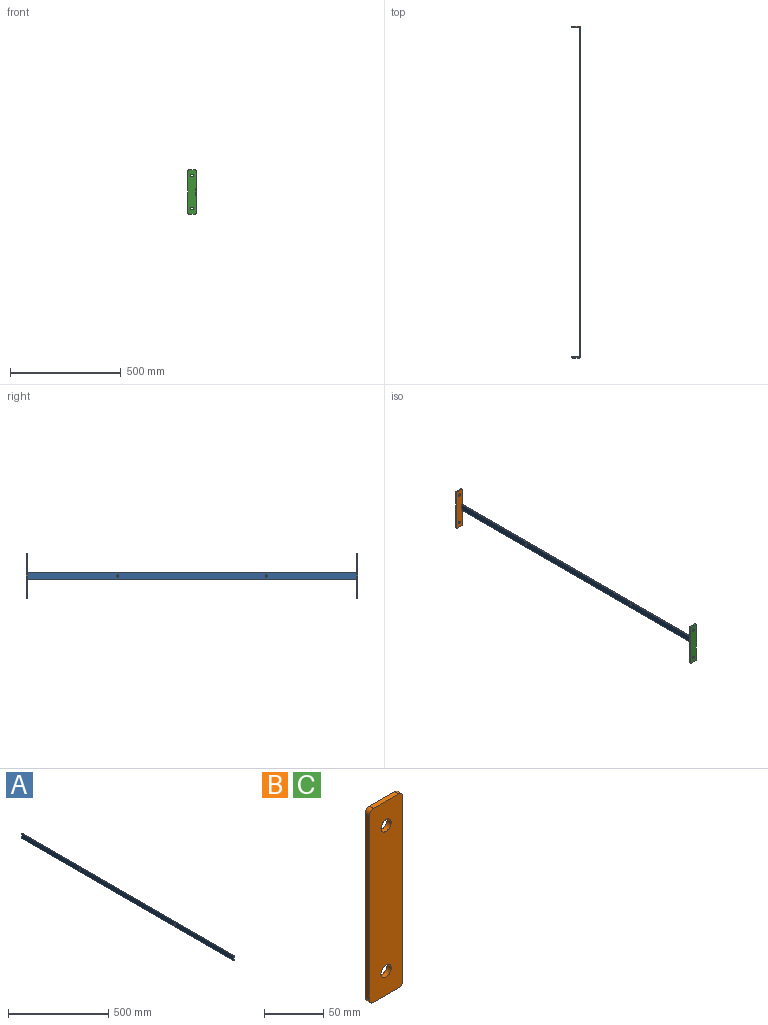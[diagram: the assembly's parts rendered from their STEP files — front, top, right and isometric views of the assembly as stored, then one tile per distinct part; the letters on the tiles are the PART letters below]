
ASSEMBLY  parts=3 mates=2
PART A: 8 faces, bbox 5x1490x30 mm
  f0: plane 30x5mm, normal (0,-1,0), area 150mm2, adj f1,f4,f6,f7
  f1: plane 1490x5mm, normal (0,0,-1), area 7450mm2, adj f0,f2,f6,f7
  f2: plane 30x5mm, normal (0,1,0), area 150mm2, adj f1,f4,f6,f7
  f3: cylinder r=5.1mm len=10.2mm, axis (-1,0,0), area 160.2mm2, adj f6,f7
  f4: plane 1490x5mm, normal (0,0,1), area 7450mm2, adj f0,f2,f6,f7
  f5: cylinder r=5.1mm len=10.2mm, axis (-1,0,0), area 160.2mm2, adj f6,f7
  f6: plane 1490x30mm, normal (1,0,0), area 44536.6mm2, adj f0,f1,f2,f3,f4,f5
  f7: plane 1490x30mm, normal (-1,0,0), area 44536.6mm2, adj f0,f1,f2,f3,f4,f5
PART B: 12 faces, bbox 40x5x200 mm
  f0: plane 190x5mm, normal (1,0,0), area 950mm2, adj f1,f9,f10,f11
  f1: cylinder r=5mm len=5mm, axis (0,1,0), area 39.3mm2, adj f0,f2,f10,f11
  f2: plane 30x5mm, normal (0,0,1), area 150mm2, adj f1,f3,f10,f11
  f3: cylinder r=5mm len=5mm, axis (0,1,0), area 39.3mm2, adj f2,f4,f10,f11
  f4: plane 190x5mm, normal (-1,0,0), area 950mm2, adj f3,f5,f10,f11
  f5: cylinder r=5mm len=5mm, axis (0,1,0), area 39.3mm2, adj f4,f6,f10,f11
  f6: plane 30x5mm, normal (0,0,-1), area 150mm2, adj f5,f9,f10,f11
  f7: cylinder r=6.1mm len=12.2mm, axis (0,1,0), area 191.6mm2, adj f10,f11
  f8: cylinder r=6.1mm len=12.2mm, axis (0,1,0), area 191.6mm2, adj f10,f11
  f9: cylinder r=5mm len=5mm, axis (0,1,0), area 39.3mm2, adj f0,f6,f10,f11
  f10: plane 200x40mm, normal (0,-1,0), area 7744.7mm2, adj f0,f1,f2,f3,f4,f5,f6,f7
  f11: plane 200x40mm, normal (0,1,0), area 7744.7mm2, adj f0,f1,f2,f3,f4,f5,f6,f7
PART C: same geometry as B
PLACE A t=(-167.18,-207.13,-44.78)mm
PLACE B t=(-20.72,872.23,127.75)mm
PLACE C t=(-20.72,-622.77,127.75)mm
MATE fastened B.f10 <-> A.f2  axis (0,-1,0) through (-162.18,867.23,108.47)mm
MATE fastened C.f11 <-> A.f0  axis (0,1,0) through (-162.18,-622.77,108.47)mm
